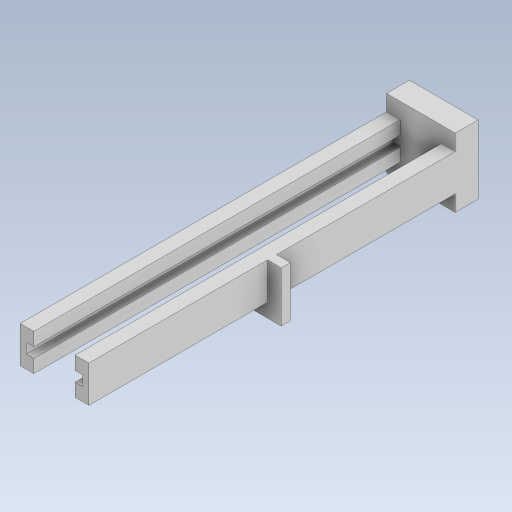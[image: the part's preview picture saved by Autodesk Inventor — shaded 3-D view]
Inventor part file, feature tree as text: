
AUTODESK INVENTOR PART (.ipt)
format: ipt  version: 2023.5 (Build 275446000, 446)  size: 157,184 bytes
history: native  units: in
note: dims shown in document units (in); Inventor stores cm internally (conversion verified against a paired STEP export)
features: extrude x4, sketch x3
ambient origin geometry x8: Origin, YZ Plane, XZ Plane, XY Plane, X Axis, Y Axis, Z Axis, Center Point
bodies: Solid1 (feature_tree)
feature tree (7):
  sketch  "Sketch1"  dims[d0=0.5906in d1=0.5906in]
  extrude  "Extrusion1"  Depth=0.5906in
  extrude  "Extrusion2"  Depth=0.315in
  extrude  "Extrusion3"  Depth=0.1181in
  extrude  "Extrusion4"  Depth=0.0866in
  sketch  "Sketch2"  dims[d2=0.1181in d3=0.315in]
  sketch  "Sketch3"  dims[d5=0.1772in d6=0.126in d7=0.0866in d8=0.1969in d9=0.0in d10=3.1496in d11=0.0in d12=0.0787in d13=0.1181in d14=0.0in d15=0.0787in d16=0.1181in d17=0.0in]
